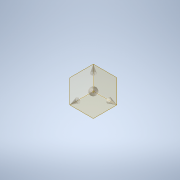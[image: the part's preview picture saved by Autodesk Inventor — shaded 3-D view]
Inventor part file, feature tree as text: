
AUTODESK INVENTOR PART (.ipt)
format: ipt  version: 2022 (Build 260153000, 153)  size: 9,568,768 bytes
history: native  units: mm
features: sketch x8, surface_op x6, plane x3, mirror x2, boolean_combine x2, other x2, loft x1, sweep x1, extrude x1, split x1
ambient origin geometry x8: Origin, YZ Plane, XZ Plane, XY Plane, X Axis, Y Axis, Z Axis, Center Point
bodies: Solid10 (feature_tree), Solid12 (feature_tree), Solid13 (feature_tree)
feature tree (27):
  sketch  "Sketch1"  dims[d3=30.0mm d27=20.0mm]
  sketch  "Sketch2"  dims[d33=7.5mm d34=2.0mm]
  plane  "Work Plane1"
  sketch  "3D Sketch1"
  sketch  "Sketch4"  dims[d35=0.0mm d36=90.0deg d37=0.0mm d38=90.0deg]
  plane  "Work Plane2"
  sketch  "Sketch6"  dims[d39=-7.5mm]
  loft  "Loft1"
  plane  "Work Plane3"
  sweep  "Sweep13"
  mirror  "Mirror3"
  mirror  "Mirror4"
  sketch  "Sketch8"  dims[d43=7.5mm d44=310.0mm d45=0.0mm d46=0.0mm d47=680.0mm d48=90.0deg d49=50.0mm d51=70.0mm d52=0.0mm d53=0.0mm d62=70.0mm d63=2184.75mm d64=3451.75mm d65=47138.5mm d66=69536.75mm d50=0.5mm d54=0.872665mm]
  boolean_combine  "Combine1"
  extrude  "Extrusion2"  TaperAngle=0.0deg  [1 undecoded]
  boolean_combine  "Combine2"
  surface_op  "Extend4"
  surface_op  "Extend5"
  surface_op  "Extend6"
  surface_op  "Extend7"
  surface_op  "Extend8"
  split  "Split1"
  sketch  "Sketch7"  dims[d42=20.0mm]
  other  "Pattern of Solid10:2"
  sketch  "3D Sketch2"
  other  "Srf1"
  surface_op  "Boundary Patch1"
note: 1 required parameter value undecoded (feature->parameter linkage not recoverable at this tier; creation-order binding heuristic only, values carry confidence <= 0.55)
